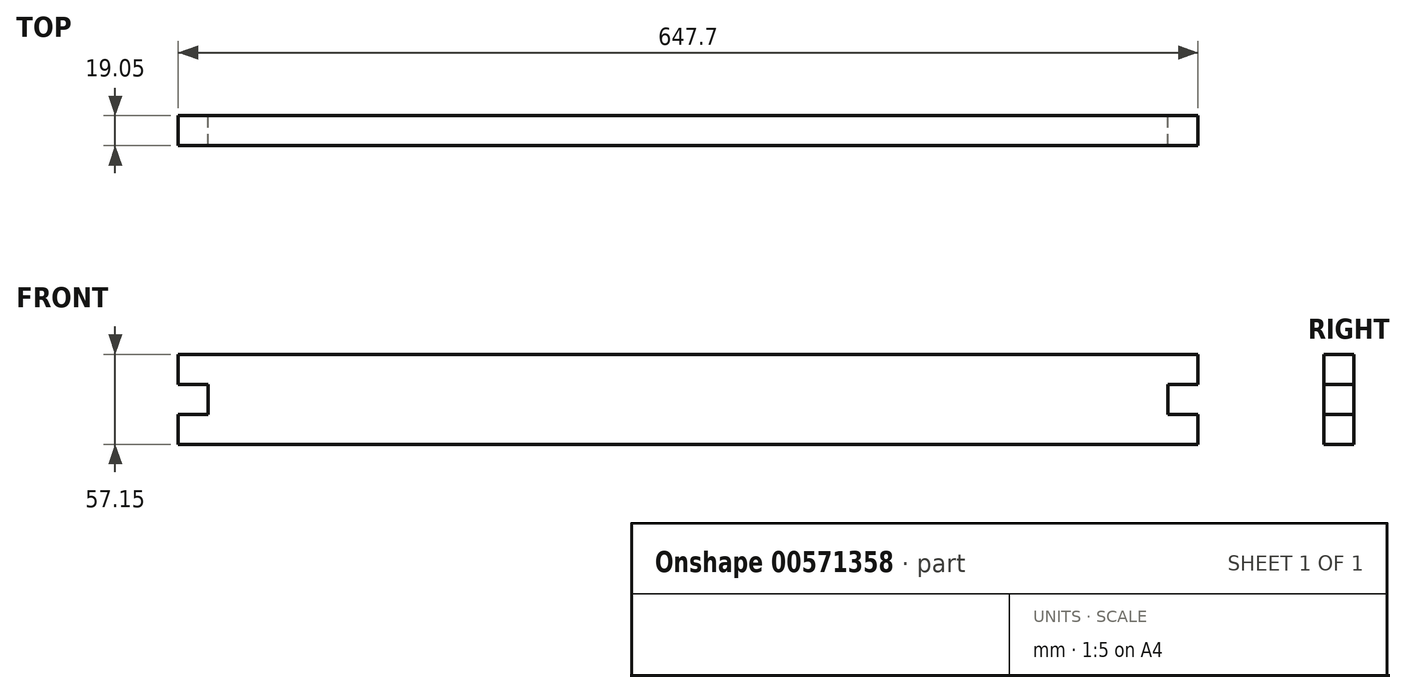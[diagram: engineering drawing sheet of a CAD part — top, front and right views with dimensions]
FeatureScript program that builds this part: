
annotation { "Feature Type Name" : "Feature", "Feature Type Description" : "" }
export const myFeature = defineFeature(function(context is Context, id is Id, definition is map)
    precondition{}
    {
        {
            var Q0;
            Q0=qCreatedBy(makeId("Front.planeOp"),FACE);
            var sketch = newSketch(context, id + "F0", { "sketchPlane" : qUnion([Q0])});
            skLineSegment(sketch, "E0", {"start": v(-296.67, -147.65) * mm, "end": v(312.93, -147.65) * mm});
            skLineSegment(sketch, "E1", {"start": v(-296.67, -204.8) * mm, "end": v(312.93, -204.8) * mm});
            skLineSegment(sketch, "E2", {"start": v(-296.67, -166.7) * mm, "end": v(-296.67, -185.75) * mm});
            skLineSegment(sketch, "E3", {"start": v(-296.67, -147.65) * mm, "end": v(-315.72, -147.65) * mm});
            skLineSegment(sketch, "E4", {"start": v(-315.72, -147.65) * mm, "end": v(-315.72, -166.7) * mm});
            skLineSegment(sketch, "E5", {"start": v(-315.72, -166.7) * mm, "end": v(-296.67, -166.7) * mm});
            skLineSegment(sketch, "E6", {"start": v(-296.67, -185.75) * mm, "end": v(-315.72, -185.75) * mm});
            skLineSegment(sketch, "E7", {"start": v(-315.72, -185.75) * mm, "end": v(-315.72, -204.8) * mm});
            skLineSegment(sketch, "E8", {"start": v(-315.72, -204.8) * mm, "end": v(-296.67, -204.8) * mm});
            skLineSegment(sketch, "E9.trimOffspring", {"start": v(-296.67, -204.8) * mm, "end": v(-296.67, -204.8) * mm});
            skLineSegment(sketch, "E10", {"start": v(331.98, -147.65) * mm, "end": v(331.98, -166.7) * mm});
            skLineSegment(sketch, "E11", {"start": v(331.98, -166.7) * mm, "end": v(312.93, -166.7) * mm});
            skLineSegment(sketch, "E12", {"start": v(312.93, -204.8) * mm, "end": v(312.93, -147.65) * mm});
            skLineSegment(sketch, "E13", {"start": v(331.98, -147.65) * mm, "end": v(312.93, -147.65) * mm});
            skLineSegment(sketch, "E14", {"start": v(312.93, -204.8) * mm, "end": v(331.98, -204.8) * mm});
            skLineSegment(sketch, "E15", {"start": v(331.98, -204.8) * mm, "end": v(331.98, -185.75) * mm});
            skLineSegment(sketch, "E16", {"start": v(331.98, -185.75) * mm, "end": v(312.93, -185.75) * mm});
            skSolve(sketch);
        }
        {
            var Q0;
            Q0=makeQuery(id+"F0.imprint","IMPRINT",FACE,{"disambiguationData":[TD([[makeQuery(id+"F0.imprint","IMPRINT",EDGE,{"derivedFrom":sQuery(id+"F0.wireOp",EDGE,"E0")}),-1.0]])]});
            var Q1;
            Q1=makeQuery(id+"F0.imprint","IMPRINT",FACE,{"disambiguationData":[TD([[makeQuery(id+"F0.imprint","IMPRINT",EDGE,{"derivedFrom":sQuery(id+"F0.wireOp",EDGE,"E10")}),-1.0]])]});
            var Q2;
            {var subQ0=sQuery(id+"F0.wireOp",EDGE,"nr3U3Fr9-u0Ao-JbR5-QgKX-yn1Y0DcPVaOF");Q2=makeQuery(id+"F0.imprint","IMPRINT",FACE,{"disambiguationData":[TD([[makeQuery(id+"F0.imprint","IMPRINT",EDGE,{"derivedFrom":subQ0}),-1.0]])]});}
            var Q3;
            {var subQ0=sQuery(id+"F0.wireOp",EDGE,"E14");Q3=makeQuery(id+"F0.imprint","IMPRINT",FACE,{"disambiguationData":[TD([[makeQuery(id+"F0.imprint","IMPRINT",EDGE,{"derivedFrom":subQ0}),1.0]])]});}
            extrude(context, id + "F1", {"entities" : qUnion([Q0, Q1, Q2, Q3]), "depth" : 19.05 * mm, "offsetDistance" : 25.4 * mm});
        }
    });
